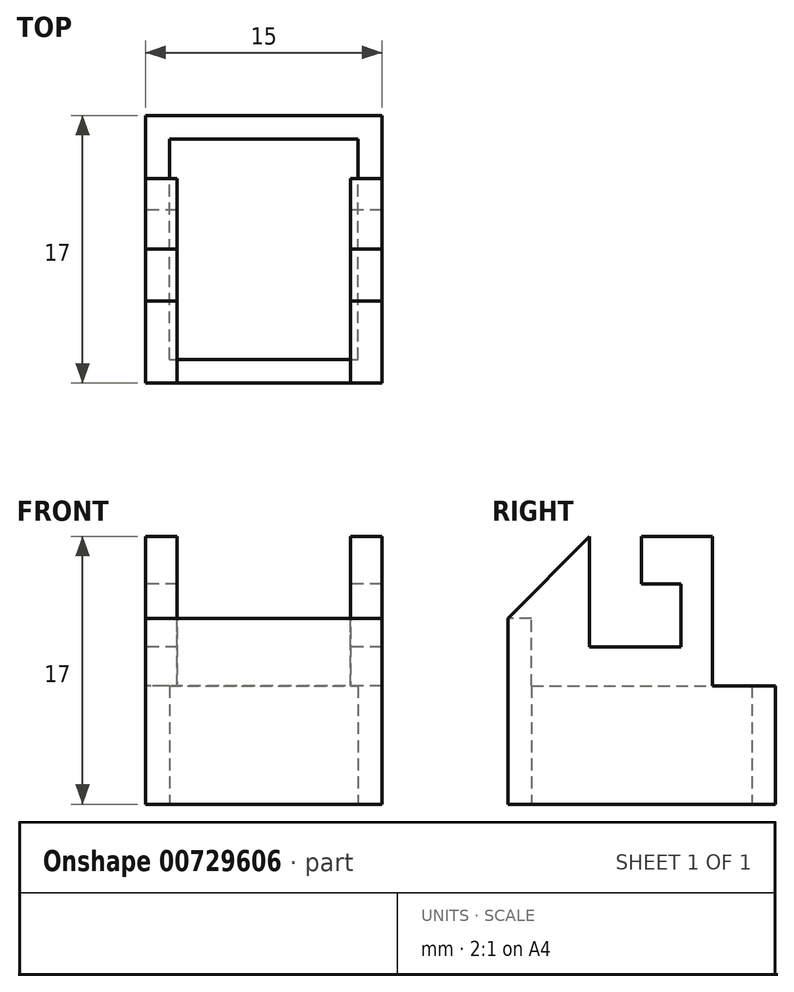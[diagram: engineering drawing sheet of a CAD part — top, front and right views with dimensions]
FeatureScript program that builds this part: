
annotation { "Feature Type Name" : "Feature", "Feature Type Description" : "" }
export const myFeature = defineFeature(function(context is Context, id is Id, definition is map)
    precondition{}
    {
        {
            var Q0;
            Q0=qCreatedBy(makeId("Right.planeOp"),FACE);
            var sketch = newSketch(context, id + "F0", { "sketchPlane" : qUnion([Q0])});
            skLineSegment(sketch, "E0", {"start": v(0, 0) * mm, "end": v(0, 7.5) * mm});
            skLineSegment(sketch, "E1", {"start": v(0, 7.5) * mm, "end": v(-4, 7.5) * mm});
            skLineSegment(sketch, "E2", {"start": v(-4, 7.5) * mm, "end": v(-4, 17) * mm});
            skLineSegment(sketch, "E3", {"start": v(-4, 17) * mm, "end": v(-8.5, 17) * mm});
            skLineSegment(sketch, "E4", {"start": v(-8.5, 17) * mm, "end": v(-8.5, 14) * mm});
            skLineSegment(sketch, "E5", {"start": v(-8.5, 14) * mm, "end": v(-6, 14) * mm});
            skLineSegment(sketch, "E6", {"start": v(-6, 14) * mm, "end": v(-6, 10) * mm});
            skLineSegment(sketch, "E7", {"start": v(-6, 10) * mm, "end": v(-11.8, 10) * mm});
            skLineSegment(sketch, "E8", {"start": v(-11.8, 10) * mm, "end": v(-11.8, 17) * mm});
            skLineSegment(sketch, "E9", {"start": v(-11.8, 17) * mm, "end": v(-17, 11.8) * mm});
            skLineSegment(sketch, "E10", {"start": v(-17, 11.8) * mm, "end": v(-17, 0) * mm});
            skLineSegment(sketch, "E11", {"start": v(-17, 0) * mm, "end": v(0, 0) * mm});
            skSolve(sketch);
        }
        {
            var Q0;
            Q0=makeQuery(id+"F0.imprint","IMPRINT",FACE,{"disambiguationData":[TD([[makeQuery(id+"F0.imprint","IMPRINT",EDGE,{"derivedFrom":sQuery(id+"F0.wireOp",EDGE,"E0")}),1.0]])]});
            extrude(context, id + "F1", {"entities" : qUnion([Q0]), "depth" : 15 * mm, "offsetDistance" : 25 * mm});
        }
        {
            var Q0;
            Q0=makeQuery(id+"F1.opExtrude","SWEPT_FACE",FACE,{"disambiguationData":[OSD([sQuery(id+"F0.wireOp",EDGE,"E11")])]});
            var sketch = newSketch(context, id + "F2", { "sketchPlane" : qUnion([Q0])});
            skLineSegment(sketch, "E12.bottom", {"start": v(1.5, 15.5) * mm, "end": v(13.5, 15.5) * mm});
            skLineSegment(sketch, "E12.top", {"start": v(1.5, 1.5) * mm, "end": v(13.5, 1.5) * mm});
            skLineSegment(sketch, "E12.left", {"start": v(1.5, 15.5) * mm, "end": v(1.5, 1.5) * mm});
            skLineSegment(sketch, "E12.right", {"start": v(13.5, 15.5) * mm, "end": v(13.5, 1.5) * mm});
            skSolve(sketch);
        }
        {
            var Q0;
            Q0 = qSketchRegion(id + "F2", true);
            extrude(context, id + "F3", {"entities" : qUnion([Q0]), "operationType" : NewBodyOperationType.REMOVE, "oppositeDirection" : true, "depth" : 7.5 * mm, "offsetDistance" : 25 * mm});
        }
        {
            var Q0;
            Q0=makeQuery(id+"F1.opExtrude","SWEPT_FACE",FACE,{"disambiguationData":[OSD([sQuery(id+"F0.wireOp",EDGE,"E3")])]});
            var sketch = newSketch(context, id + "F4", { "sketchPlane" : qUnion([Q0])});
            skLineSegment(sketch, "E13.bottom", {"start": v(2, -1.5) * mm, "end": v(13, -1.5) * mm});
            skLineSegment(sketch, "E13.top", {"start": v(2, -15.5) * mm, "end": v(13, -15.5) * mm});
            skLineSegment(sketch, "E13.left", {"start": v(2, -1.5) * mm, "end": v(2, -15.5) * mm});
            skLineSegment(sketch, "E13.right", {"start": v(13, -1.5) * mm, "end": v(13, -15.5) * mm});
            skSolve(sketch);
        }
        {
            var Q0;
            Q0 = qSketchRegion(id + "F4", true);
            extrude(context, id + "F5", {"entities" : qUnion([Q0]), "operationType" : NewBodyOperationType.REMOVE, "oppositeDirection" : true, "depth" : 17 * mm, "offsetDistance" : 25 * mm});
        }
        {
            var Q0;
            {var subQ1=sQuery(id+"F0.wireOp",EDGE,"E3");Q0=makeQuery(id+"F5.boolean.opBoolean","SPLIT",FACE,{"disambiguationData":[TD([makeQuery(id+"F5.opExtrude","SWEPT_FACE",FACE,{"disambiguationData":[OSD([sQuery(id+"F4.wireOp",EDGE,"E13.left")])]})])],"derivedFrom":makeQuery(id+"F1.opExtrude","SWEPT_FACE",FACE,{"disambiguationData":[OSD([subQ1])]})});}
            var sketch = newSketch(context, id + "F6", { "sketchPlane" : qUnion([Q0])});
            skLineSegment(sketch, "E14.bottom", {"start": v(2, -15.5) * mm, "end": v(13, -15.5) * mm});
            skLineSegment(sketch, "E14.top", {"start": v(2, -17) * mm, "end": v(13, -17) * mm});
            skLineSegment(sketch, "E14.left", {"start": v(2, -15.5) * mm, "end": v(2, -17) * mm});
            skLineSegment(sketch, "E14.right", {"start": v(13, -15.5) * mm, "end": v(13, -17) * mm});
            skSolve(sketch);
        }
        {
            var Q0;
            Q0 = qSketchRegion(id + "F6", true);
            extrude(context, id + "F7", {"entities" : qUnion([Q0]), "operationType" : NewBodyOperationType.REMOVE, "oppositeDirection" : true, "depth" : 5.2 * mm, "offsetDistance" : 25 * mm});
        }
    });
